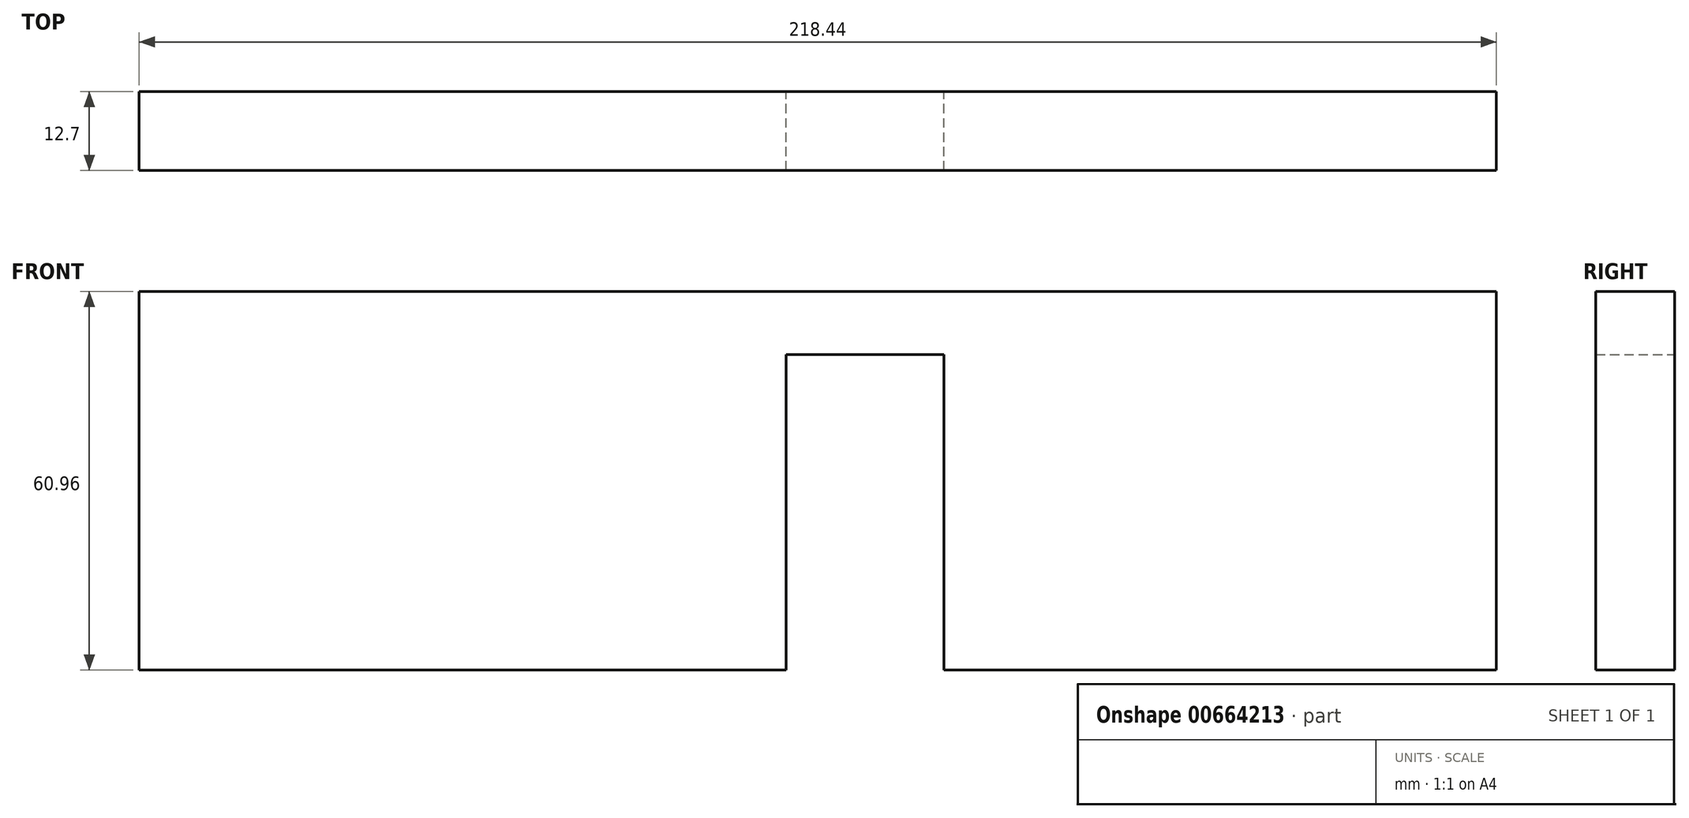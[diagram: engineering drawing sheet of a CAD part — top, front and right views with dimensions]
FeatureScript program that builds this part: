
annotation { "Feature Type Name" : "Feature", "Feature Type Description" : "" }
export const myFeature = defineFeature(function(context is Context, id is Id, definition is map)
    precondition{}
    {
        {
            var Q0;
            Q0=qCreatedBy(makeId("Front.planeOp"),FACE);
            var sketch = newSketch(context, id + "F0", { "sketchPlane" : qUnion([Q0])});
            skLineSegment(sketch, "E0.bottom", {"start": v(0, 0) * mm, "end": v(104.14, 0) * mm});
            skLineSegment(sketch, "E0.top", {"start": v(0, 60.96) * mm, "end": v(218.44, 60.96) * mm});
            skLineSegment(sketch, "E0.left", {"start": v(0, 0) * mm, "end": v(0, 60.96) * mm});
            skLineSegment(sketch, "E0.right", {"start": v(218.44, 0) * mm, "end": v(218.44, 60.96) * mm});
            skLineSegment(sketch, "E1.top", {"start": v(104.14, 50.8) * mm, "end": v(129.54, 50.8) * mm});
            skLineSegment(sketch, "E1.left", {"start": v(104.14, 0) * mm, "end": v(104.14, 50.8) * mm});
            skLineSegment(sketch, "E1.right", {"start": v(129.54, 0) * mm, "end": v(129.54, 50.8) * mm});
            skLineSegment(sketch, "E2.trimOffspring", {"start": v(129.54, 0) * mm, "end": v(218.44, 0) * mm});
            skSolve(sketch);
        }
        {
            var Q0;
            Q0 = qSketchRegion(id + "F0", true);
            extrude(context, id + "F1", {"entities" : qUnion([Q0]), "depth" : 12.7 * mm, "offsetDistance" : 25.4 * mm});
        }
    });
